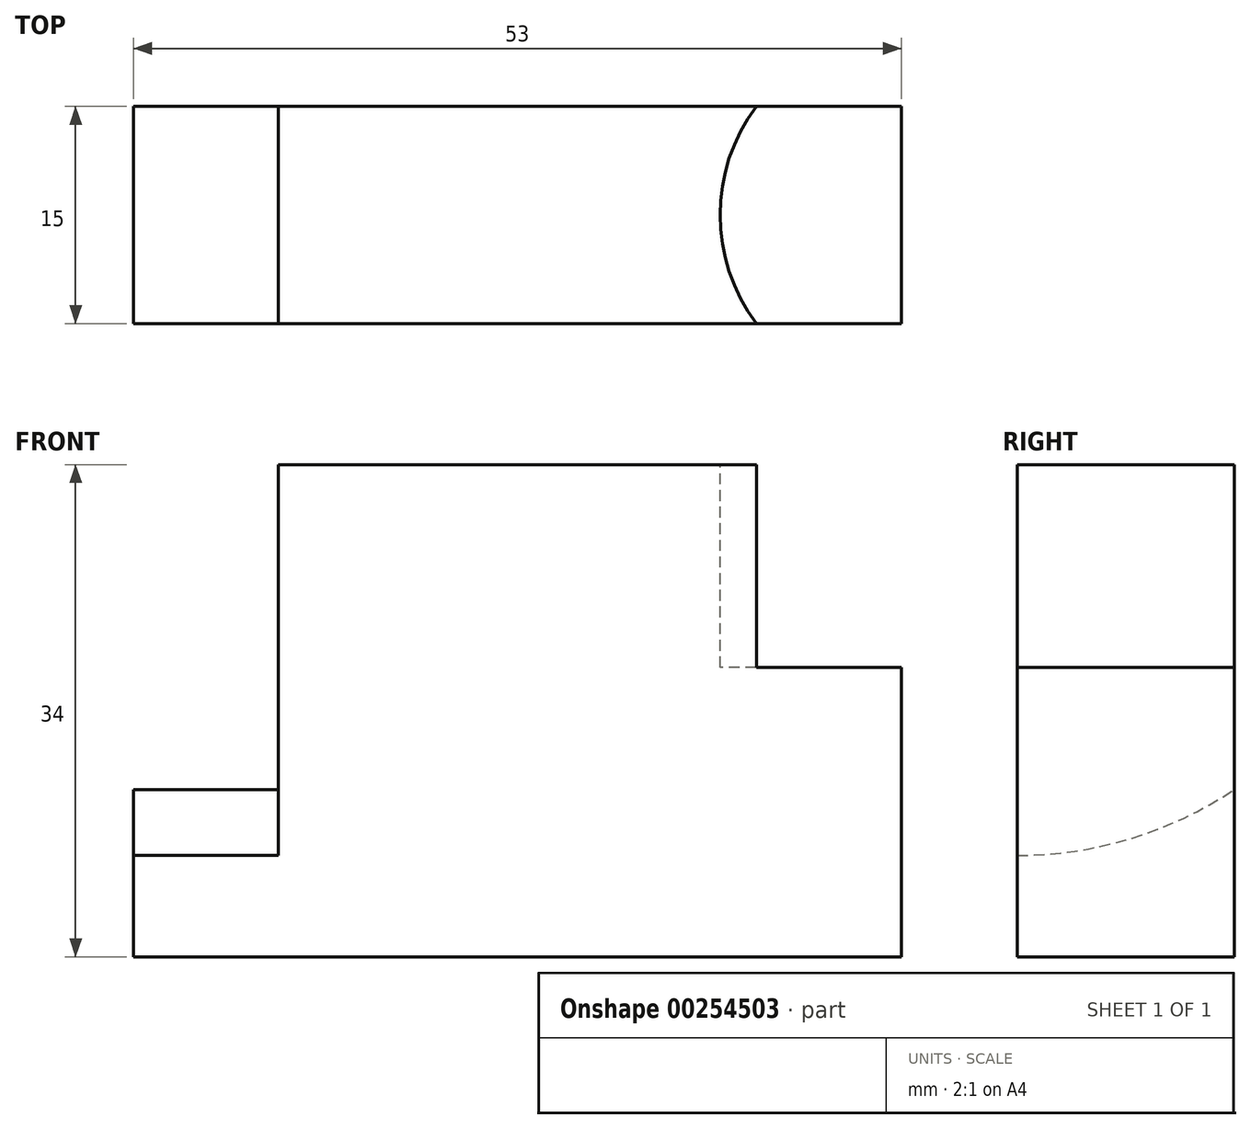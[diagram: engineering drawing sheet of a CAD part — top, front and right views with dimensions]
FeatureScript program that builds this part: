
annotation { "Feature Type Name" : "Feature", "Feature Type Description" : "" }
export const myFeature = defineFeature(function(context is Context, id is Id, definition is map)
    precondition{}
    {
        {
            var Q0;
            Q0=qCreatedBy(makeId("Front.planeOp"),FACE);
            var sketch = newSketch(context, id + "F0", { "sketchPlane" : qUnion([Q0])});
            skLineSegment(sketch, "E0.bottom", {"start": v(-24.14, 18.29) * mm, "end": v(28.86, 18.29) * mm});
            skLineSegment(sketch, "E0.top", {"start": v(-24.14, -15.71) * mm, "end": v(28.86, -15.71) * mm});
            skLineSegment(sketch, "E0.left", {"start": v(-24.14, 18.29) * mm, "end": v(-24.14, -15.71) * mm});
            skLineSegment(sketch, "E0.right", {"start": v(28.86, 18.29) * mm, "end": v(28.86, -15.71) * mm});
            skSolve(sketch);
        }
        {
            var Q0;
            Q0=makeQuery(id+"F0.imprint","IMPRINT",FACE,{"disambiguationData":[TD([[makeQuery(id+"F0.imprint","IMPRINT",EDGE,{"derivedFrom":sQuery(id+"F0.wireOp",EDGE,"E0.bottom")}),-1.0]])]});
            extrude(context, id + "F1", {"entities" : qUnion([Q0]), "depth" : 15 * mm, "offsetDistance" : 25 * mm});
        }
        {
            var Q0;
            Q0=makeQuery(id+"F1.opExtrude","SWEPT_FACE",FACE,{"disambiguationData":[OSD([sQuery(id+"F0.wireOp",EDGE,"E0.left")])]});
            var sketch = newSketch(context, id + "F2", { "sketchPlane" : qUnion([Q0])});
            skCircle(sketch, "E1", {"center": v(15, 18.29) * mm, "radius": 27 * mm});
            skSolve(sketch);
        }
        {
            var Q0;
            Q0 = qSketchRegion(id + "F2", true);
            extrude(context, id + "F3", {"entities" : qUnion([Q0]), "operationType" : NewBodyOperationType.REMOVE, "oppositeDirection" : true, "depth" : 10 * mm, "offsetDistance" : 25 * mm});
        }
        {
            var Q0;
            Q0=makeQuery(id+"F1.opExtrude","SWEPT_FACE",FACE,{"disambiguationData":[OSD([sQuery(id+"F0.wireOp",EDGE,"E0.bottom")])]});
            var sketch = newSketch(context, id + "F4", { "sketchPlane" : qUnion([Q0])});
            skCircle(sketch, "E2", {"center": v(28.86, -7.5) * mm, "radius": 12.5 * mm});
            skSolve(sketch);
        }
        {
            var Q0;
            {var subQ0=sQuery(id+"F4.wireOp",EDGE,"E2");var subQ1=makeQuery(id+"F1.opExtrude","SWEPT_EDGE",EDGE,{"disambiguationData":[OSD([sQuery(id+"F0.wireOp",EDGE,"E0.bottom"),sQuery(id+"F0.wireOp",EDGE,"E0.right")])]});var subQ2=makeQuery(id+"F4.imprint","INTERSECT",VERTEX,{"disambiguationData":[OD(0.0)],"derivedFrom":[subQ1,subQ0]});Q0=makeQuery(id+"F4.imprint","IMPRINT",FACE,{"disambiguationData":[TD([[makeQuery(id+"F4.imprint","IMPRINT",EDGE,{"disambiguationData":[TD([[subQ2,-1.0]])],"derivedFrom":subQ0}),1.0]])]});}
            extrude(context, id + "F5", {"entities" : qUnion([Q0]), "operationType" : NewBodyOperationType.REMOVE, "oppositeDirection" : true, "depth" : 14 * mm, "offsetDistance" : 25 * mm});
        }
    });
